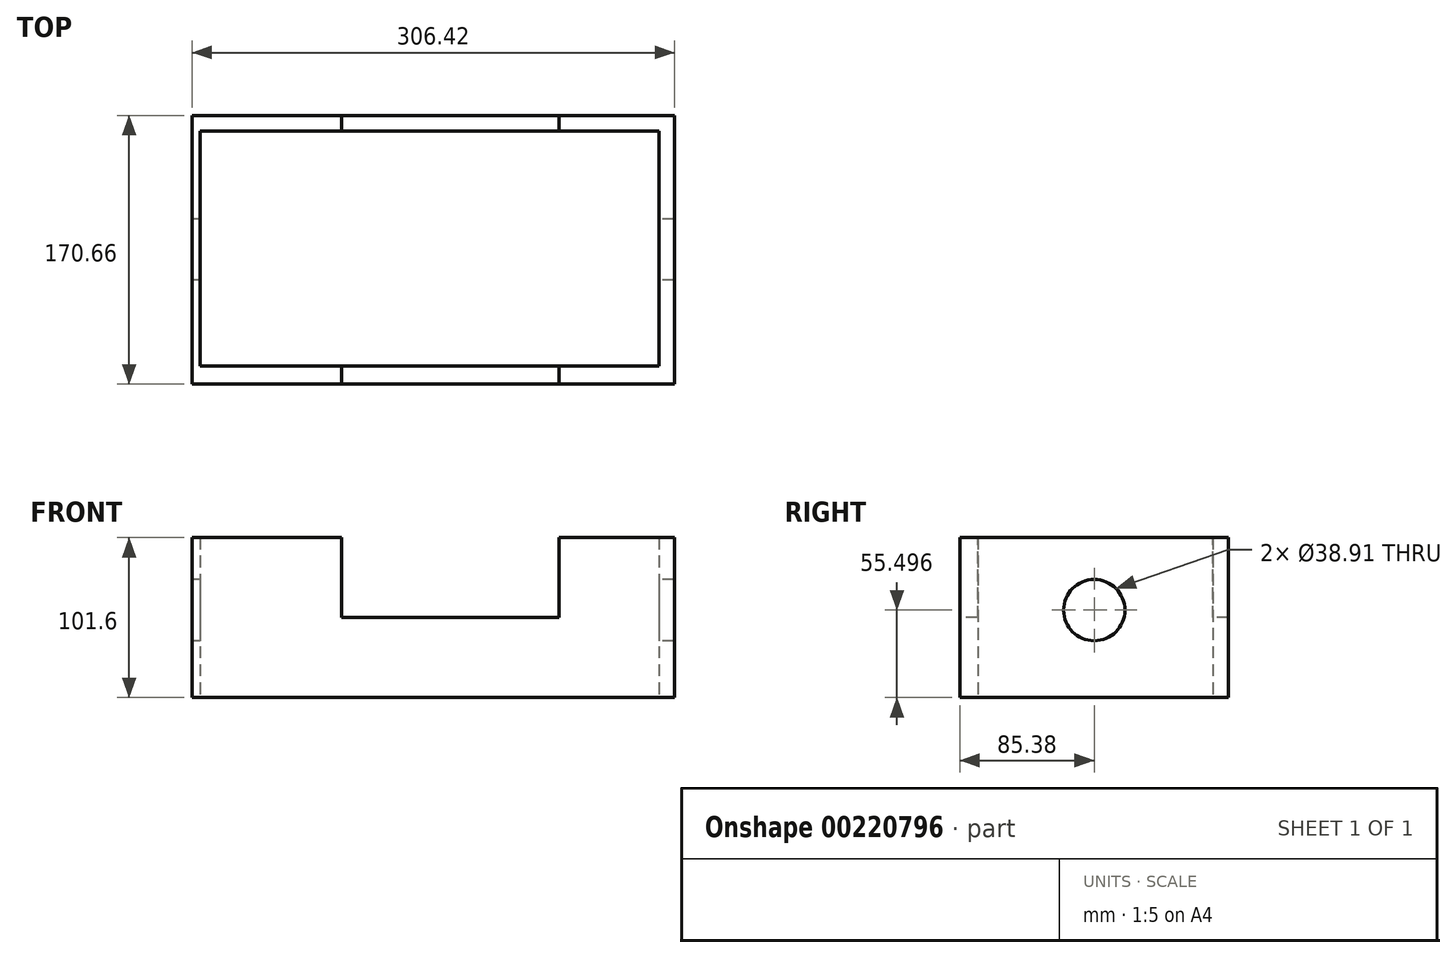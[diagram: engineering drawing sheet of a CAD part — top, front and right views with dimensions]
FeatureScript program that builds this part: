
annotation { "Feature Type Name" : "Feature", "Feature Type Description" : "" }
export const myFeature = defineFeature(function(context is Context, id is Id, definition is map)
    precondition{}
    {
        {
            var Q0;
            Q0=qCreatedBy(makeId("Top.planeOp"),FACE);
            var sketch = newSketch(context, id + "F0", { "sketchPlane" : qUnion([Q0])});
            skLineSegment(sketch, "E0.bottom", {"start": v(-154.32, -85.38) * mm, "end": v(152.1, -85.38) * mm});
            skLineSegment(sketch, "E0.top", {"start": v(-154.32, 85.28) * mm, "end": v(152.1, 85.28) * mm});
            skLineSegment(sketch, "E0.left", {"start": v(-154.32, -85.38) * mm, "end": v(-154.32, 85.28) * mm});
            skLineSegment(sketch, "E0.right", {"start": v(152.1, -85.38) * mm, "end": v(152.1, 85.28) * mm});
            skLineSegment(sketch, "E1.bottom", {"start": v(-149.08, -74.02) * mm, "end": v(142.19, -74.02) * mm});
            skLineSegment(sketch, "E1.top", {"start": v(-149.08, 75.39) * mm, "end": v(142.19, 75.39) * mm});
            skLineSegment(sketch, "E1.left", {"start": v(-149.08, -74.02) * mm, "end": v(-149.08, 75.39) * mm});
            skLineSegment(sketch, "E1.right", {"start": v(142.19, -74.02) * mm, "end": v(142.19, 75.39) * mm});
            skSolve(sketch);
        }
        {
            var Q0;
            Q0=makeQuery(id+"F0.imprint","IMPRINT",FACE,{"disambiguationData":[TD([[makeQuery(id+"F0.imprint","IMPRINT",EDGE,{"derivedFrom":sQuery(id+"F0.wireOp",EDGE,"E0.bottom")}),1.0]])]});
            extrude(context, id + "F1", {"entities" : qUnion([Q0]), "depth" : 101.6 * mm});
        }
        {
            var Q0;
            Q0=makeQuery(id+"F1.opExtrude","SWEPT_FACE",FACE,{"disambiguationData":[OSD([sQuery(id+"F0.wireOp",EDGE,"E0.bottom")])]});
            var sketch = newSketch(context, id + "F2", { "sketchPlane" : qUnion([Q0])});
            skPoint(sketch, "E2.oppositeSnap0", {"position": v(-154.32, 50.8) * mm});
            skLineSegment(sketch, "E2.bottom", {"start": v(-59.18, 118.68) * mm, "end": v(78.9, 118.68) * mm});
            skLineSegment(sketch, "E2.top", {"start": v(-59.18, 50.8) * mm, "end": v(78.9, 50.8) * mm});
            skLineSegment(sketch, "E2.left", {"start": v(-59.18, 118.68) * mm, "end": v(-59.18, 50.8) * mm});
            skLineSegment(sketch, "E2.right", {"start": v(78.9, 118.68) * mm, "end": v(78.9, 50.8) * mm});
            skSolve(sketch);
        }
        {
            var Q0;
            Q0 = qSketchRegion(id + "F2", true);
            extrude(context, id + "F3", {"entities" : qUnion([Q0]), "operationType" : NewBodyOperationType.ADD, "depth" : 25.4 * mm});
        }
        {
            var Q0;
            Q0=makeQuery(id+"F3.opExtrude","CAP_FACE",FACE,{"disambiguationData":[OSD([sQuery(id+"F2.wireOp",EDGE,"E2.bottom"),sQuery(id+"F2.wireOp",EDGE,"E2.top"),sQuery(id+"F2.wireOp",EDGE,"E2.left"),sQuery(id+"F2.wireOp",EDGE,"E2.right")])],"isStart":false});
            extrude(context, id + "F4", {"entities" : qUnion([Q0]), "operationType" : NewBodyOperationType.REMOVE, "oppositeDirection" : true, "depth" : 219.2 * mm});
        }
        {
            var Q0;
            Q0=makeQuery(id+"F1.opExtrude","SWEPT_FACE",FACE,{"disambiguationData":[OSD([sQuery(id+"F0.wireOp",EDGE,"E0.left")])]});
            var sketch = newSketch(context, id + "F5", { "sketchPlane" : qUnion([Q0])});
            skCircle(sketch, "E3", {"center": v(0, 55.5) * mm, "radius": 19.46 * mm});
            skSolve(sketch);
        }
        {
            var Q0;
            Q0 = qSketchRegion(id + "F5", true);
            extrude(context, id + "F6", {"entities" : qUnion([Q0]), "operationType" : NewBodyOperationType.ADD, "depth" : 25.4 * mm});
        }
        {
            var Q0;
            Q0=makeQuery(id+"F6.opExtrude","CAP_FACE",FACE,{"disambiguationData":[OSD([sQuery(id+"F5.wireOp",EDGE,"E3")])],"isStart":false});
            extrude(context, id + "F7", {"entities" : qUnion([Q0]), "operationType" : NewBodyOperationType.REMOVE, "oppositeDirection" : true, "depth" : 393.7 * mm});
        }
    });
